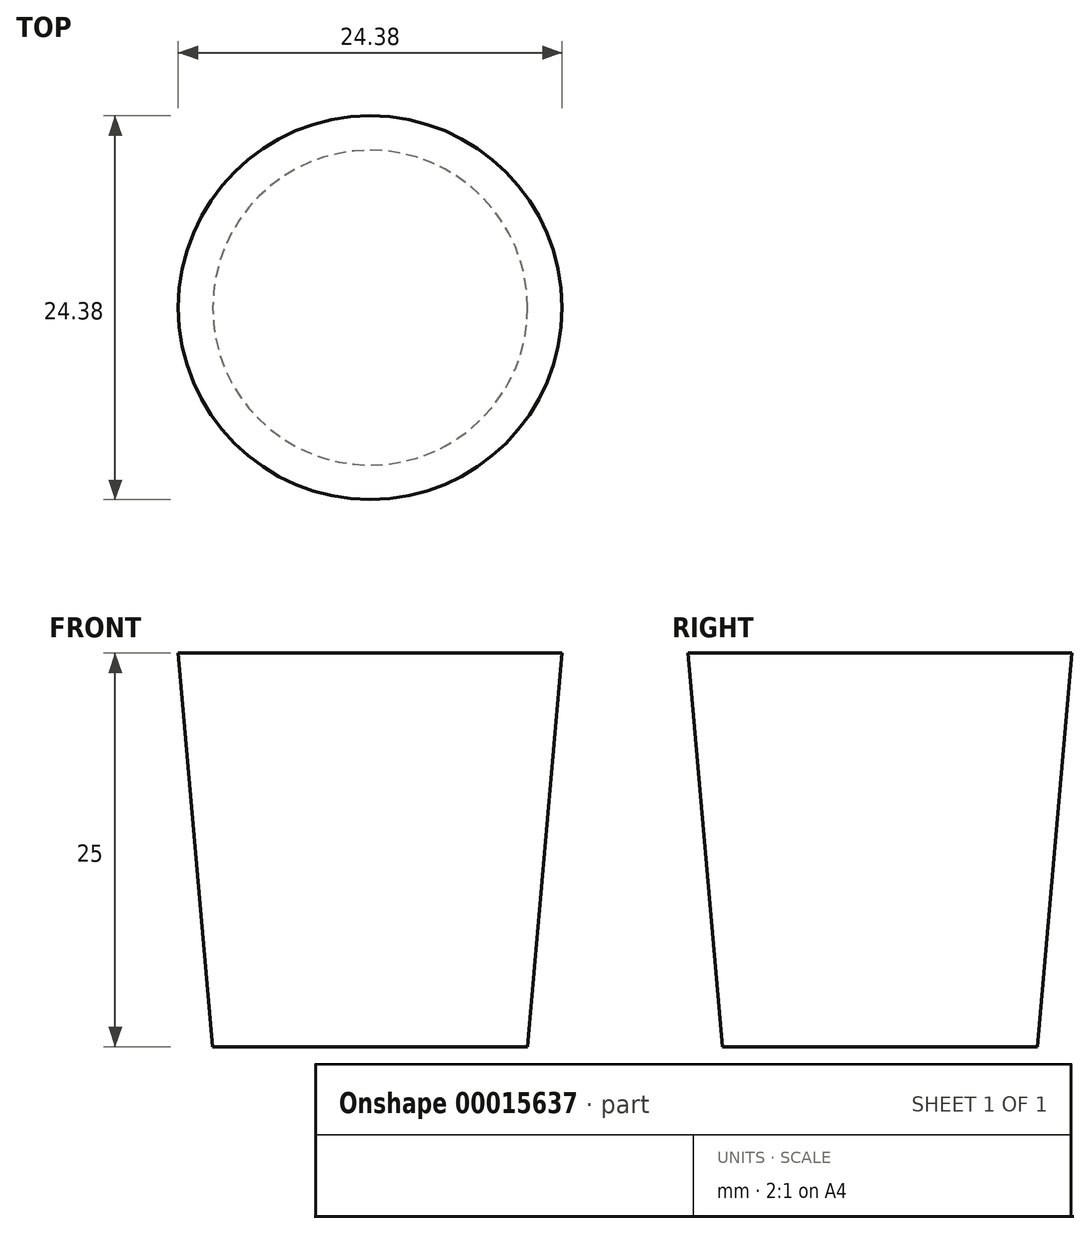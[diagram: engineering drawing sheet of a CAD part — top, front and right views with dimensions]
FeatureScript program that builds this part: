
annotation { "Feature Type Name" : "Feature", "Feature Type Description" : "" }
export const myFeature = defineFeature(function(context is Context, id is Id, definition is map)
    precondition{}
    {
        {
            var Q0;
            Q0=qCreatedBy(makeId("Top.planeOp"),FACE);
            var sketch = newSketch(context, id + "F0", { "sketchPlane" : qUnion([Q0])});
            skCircle(sketch, "E0", {"center": v(0, 0) * mm, "radius": 10 * mm});
            skSolve(sketch);
        }
        {
            var Q0;
            Q0=makeQuery(id+"F0.imprint","IMPRINT",FACE,{"disambiguationData":[TD([[makeQuery(id+"F0.imprint","IMPRINT",EDGE,{"derivedFrom":sQuery(id+"F0.wireOp",EDGE,"E0")}),1.0]])]});
            extrude(context, id + "F1", {"entities" : qUnion([Q0]), "depth" : 25 * mm, "hasDraft" : true, "draftAngle" : 5 * degree});
        }
    });
